# Revit family: C_PPB75G_2DO_CAD_MULT_Prod
name_source: partatom
category: Detail Items
revit_build: Autodesk Revit 2015 (Build: 20140606_1530(x64)
units: mm (PartAtom-declared; Revit-internal decimal feet)

## types (4) — shared parameters
Density = 0.91 kg
Description = Post bases
EPD = https://www.strongtie.eu
ETA / DoP = https://www.strongtie.eu
Manufacturer = Simpson Strong-Tie
Model = PPB75G
Model Disclaimer = Contact Simpson Strong-Tie Company  for more information
Model ID = 0204926248184546886051519115961407564608
Name = PPB75G
ObjectType = PPB75G
Product Material = HotDipGalvanised
Product Type = Post bases
Reference = PPB75G
Technical datasheet = https://www.strongtie.eu
URL = www.strongtie.eu
UniClass Number = Pr_20_29_31_44
UniClass Title = Joist hangers

## per-type parameters (varying)
| type | _visiblefront | _visibleleft | _visibleright | _visibletop |
| SST_PPB75G_Front | Yes | No | No | No |
| SST_PPB75G_Top | No | No | No | Yes |
| SST_PPB75G_Left | No | Yes | No | No |
| SST_PPB75G_Right | No | No | Yes | No |

## geometry (parser evidence)
native form markers: Blend x2, Sweep x1
no freeform markers — native parametric forms only
